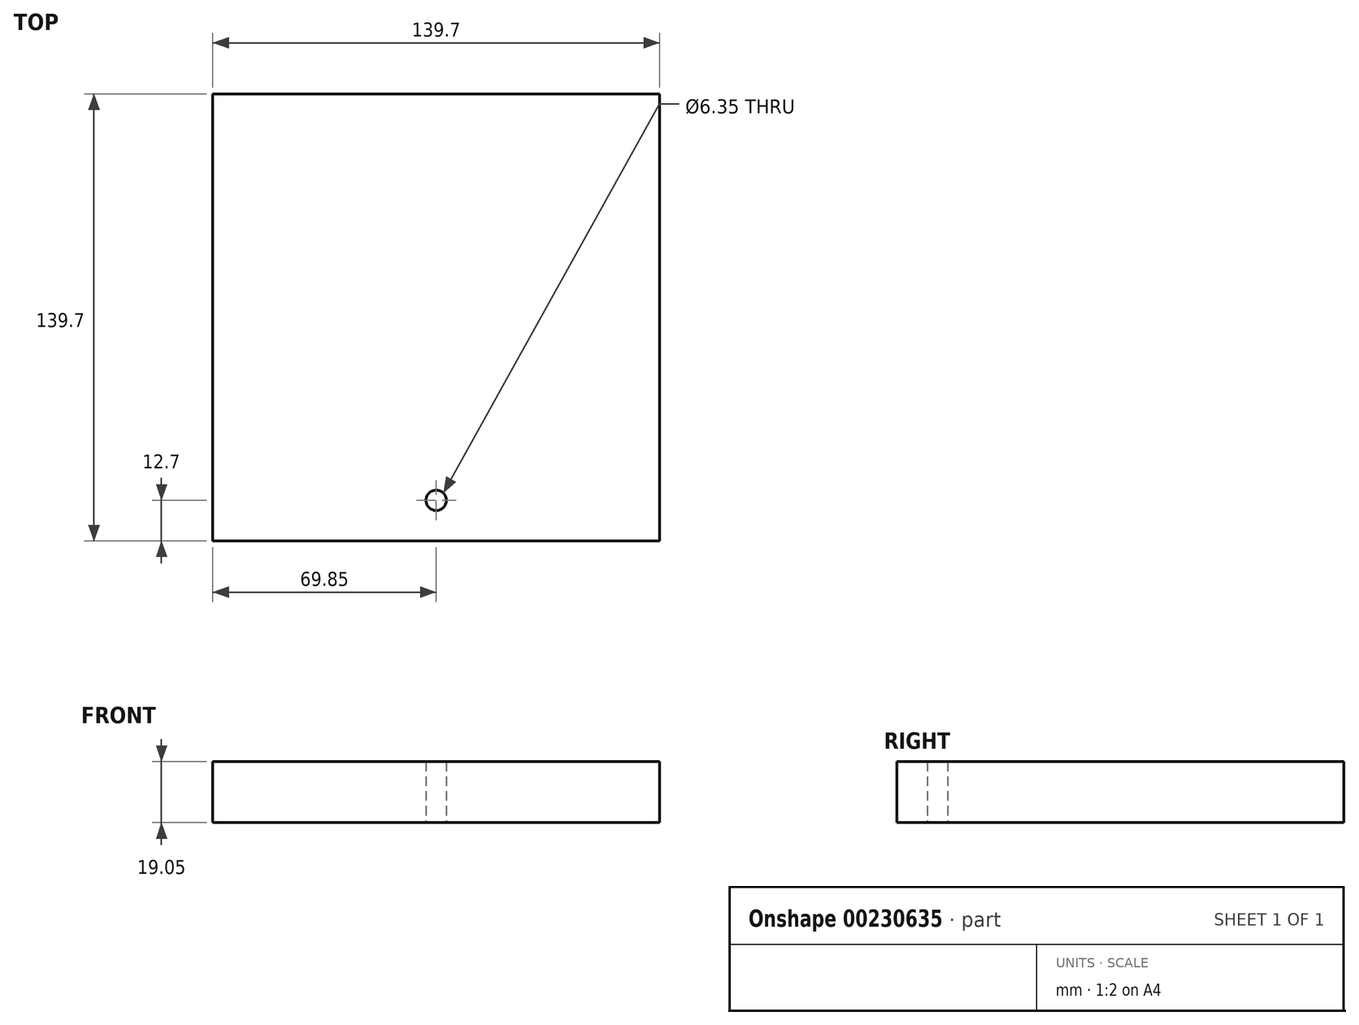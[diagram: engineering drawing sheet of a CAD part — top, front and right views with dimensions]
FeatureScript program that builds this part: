
annotation { "Feature Type Name" : "Feature", "Feature Type Description" : "" }
export const myFeature = defineFeature(function(context is Context, id is Id, definition is map)
    precondition{}
    {
        {
            var Q0;
            Q0=qCreatedBy(makeId("Top.planeOp"),FACE);
            var sketch = newSketch(context, id + "F0", { "sketchPlane" : qUnion([Q0])});
            skLineSegment(sketch, "E0.bottom", {"start": v(69.85, 69.85) * mm, "end": v(-69.85, 69.85) * mm});
            skLineSegment(sketch, "E0.top", {"start": v(69.85, -69.85) * mm, "end": v(-69.85, -69.85) * mm});
            skLineSegment(sketch, "E0.left", {"start": v(69.85, 69.85) * mm, "end": v(69.85, -69.85) * mm});
            skLineSegment(sketch, "E0.right", {"start": v(-69.85, 69.85) * mm, "end": v(-69.85, -69.85) * mm});
            skPoint(sketch, "E0.middle", {"position": v(0, 0) * mm});
            skPoint(sketch, "E1.endSnap0", {"position": v(0, -69.85) * mm});
            skCircle(sketch, "E2", {"center": v(0, -57.15) * mm, "radius": 3.18 * mm});
            skSolve(sketch);
        }
        {
            var Q0;
            Q0=makeQuery(id+"F0.imprint","IMPRINT",FACE,{"disambiguationData":[TD([[makeQuery(id+"F0.imprint","IMPRINT",EDGE,{"derivedFrom":sQuery(id+"F0.wireOp",EDGE,"E0.bottom")}),1.0]])]});
            extrude(context, id + "F1", {"entities" : qUnion([Q0]), "depth" : 19.05 * mm});
        }
    });
